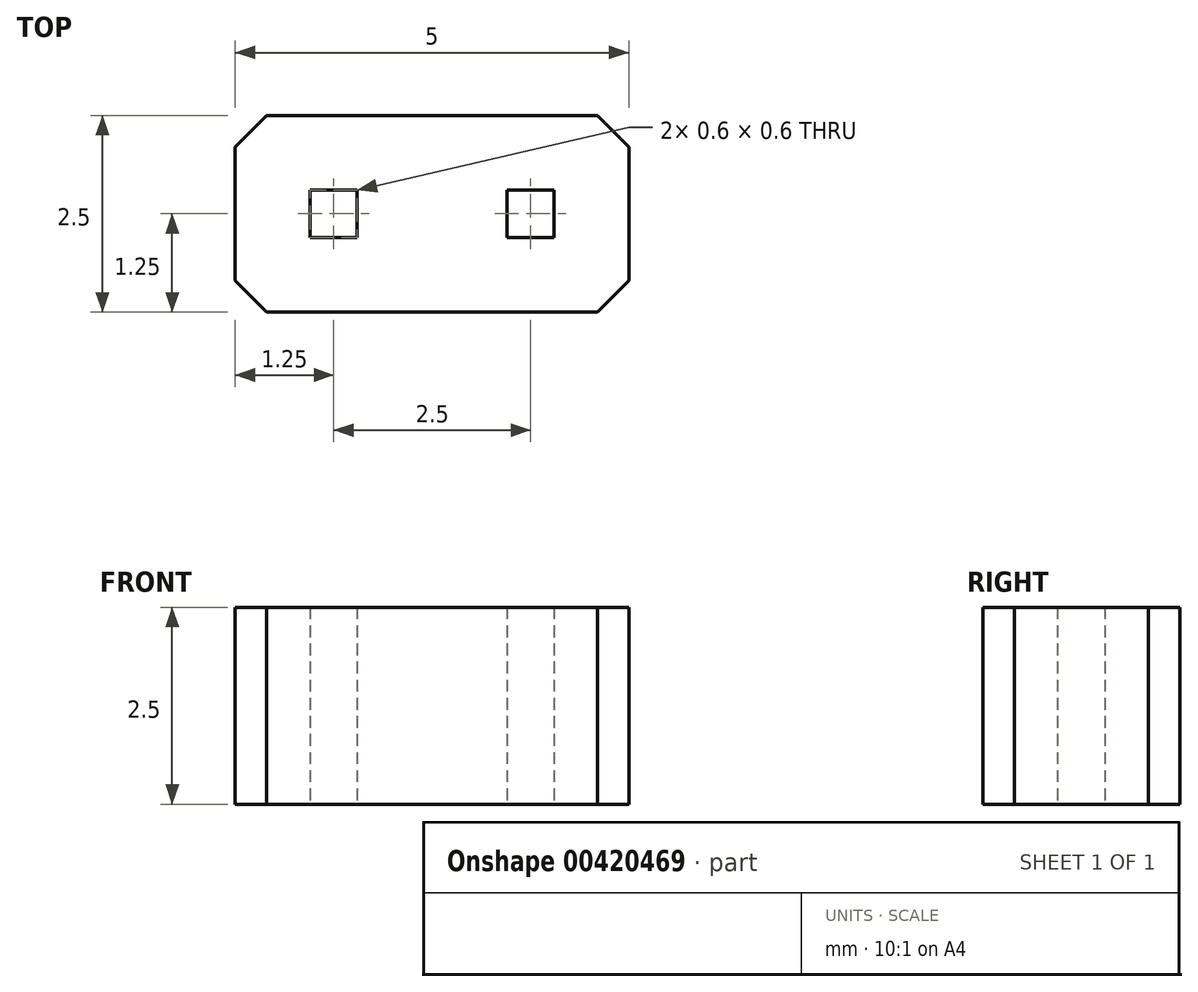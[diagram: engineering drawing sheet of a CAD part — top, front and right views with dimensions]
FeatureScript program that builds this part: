
annotation { "Feature Type Name" : "Feature", "Feature Type Description" : "" }
export const myFeature = defineFeature(function(context is Context, id is Id, definition is map)
    precondition{}
    {
        {
            var Q0;
            Q0=qCreatedBy(makeId("Top.planeOp"),FACE);
            var sketch = newSketch(context, id + "F0", { "sketchPlane" : qUnion([Q0])});
            skLineSegment(sketch, "E0.bottom", {"start": v(0, 2.5) * mm, "end": v(5, 2.5) * mm});
            skLineSegment(sketch, "E0.top", {"start": v(0, 0) * mm, "end": v(5, 0) * mm});
            skLineSegment(sketch, "E0.left", {"start": v(0, 2.5) * mm, "end": v(0, 0) * mm});
            skLineSegment(sketch, "E0.right", {"start": v(5, 2.5) * mm, "end": v(5, 0) * mm});
            skLineSegment(sketch, "E1", {"start": v(2.5, 2.5) * mm, "end": v(2.5, 0) * mm, "construction": true});
            skLineSegment(sketch, "E2.bottom", {"start": v(0.95, 1.55) * mm, "end": v(1.55, 1.55) * mm});
            skLineSegment(sketch, "E2.top", {"start": v(0.95, 0.95) * mm, "end": v(1.55, 0.95) * mm});
            skLineSegment(sketch, "E2.left", {"start": v(0.95, 1.55) * mm, "end": v(0.95, 0.95) * mm});
            skLineSegment(sketch, "E2.right", {"start": v(1.55, 1.55) * mm, "end": v(1.55, 0.95) * mm});
            skLineSegment(sketch, "E3.MirrorCS", {"start": v(3.45, 1.55) * mm, "end": v(3.45, 0.95) * mm});
            skLineSegment(sketch, "E4.MirrorCS", {"start": v(4.05, 1.55) * mm, "end": v(4.05, 0.95) * mm});
            skLineSegment(sketch, "E5.MirrorCS", {"start": v(4.05, 0.95) * mm, "end": v(3.45, 0.95) * mm});
            skLineSegment(sketch, "E6.MirrorCS", {"start": v(4.05, 1.55) * mm, "end": v(3.45, 1.55) * mm});
            skSolve(sketch);
        }
        {
            var Q0;
            Q0 = qSketchRegion(id + "F0", true);
            extrude(context, id + "F1", {"entities" : qUnion([Q0]), "depth" : 2.5 * mm});
        }
        {
            var Q0;
            Q0=makeQuery(id+"F1.opExtrude","SWEPT_EDGE",EDGE,{"disambiguationData":[OSD([sQuery(id+"F0.wireOp",EDGE,"E0.bottom"),sQuery(id+"F0.wireOp",EDGE,"E0.left")])]});
            var Q1;
            Q1=makeQuery(id+"F1.opExtrude","SWEPT_EDGE",EDGE,{"disambiguationData":[OSD([sQuery(id+"F0.wireOp",EDGE,"E0.top"),sQuery(id+"F0.wireOp",EDGE,"E0.left")])]});
            var Q2;
            Q2=makeQuery(id+"F1.opExtrude","SWEPT_EDGE",EDGE,{"disambiguationData":[OSD([sQuery(id+"F0.wireOp",EDGE,"E0.top"),sQuery(id+"F0.wireOp",EDGE,"E0.right")])]});
            var Q3;
            Q3=makeQuery(id+"F1.opExtrude","SWEPT_EDGE",EDGE,{"disambiguationData":[OSD([sQuery(id+"F0.wireOp",EDGE,"E0.bottom"),sQuery(id+"F0.wireOp",EDGE,"E0.right")])]});
            chamfer(context, id + "F2", {"entities" : qUnion([Q0, Q1, Q2, Q3]), "width" : 0.4 * mm, "tangentPropagation" : true});
        }
    });
